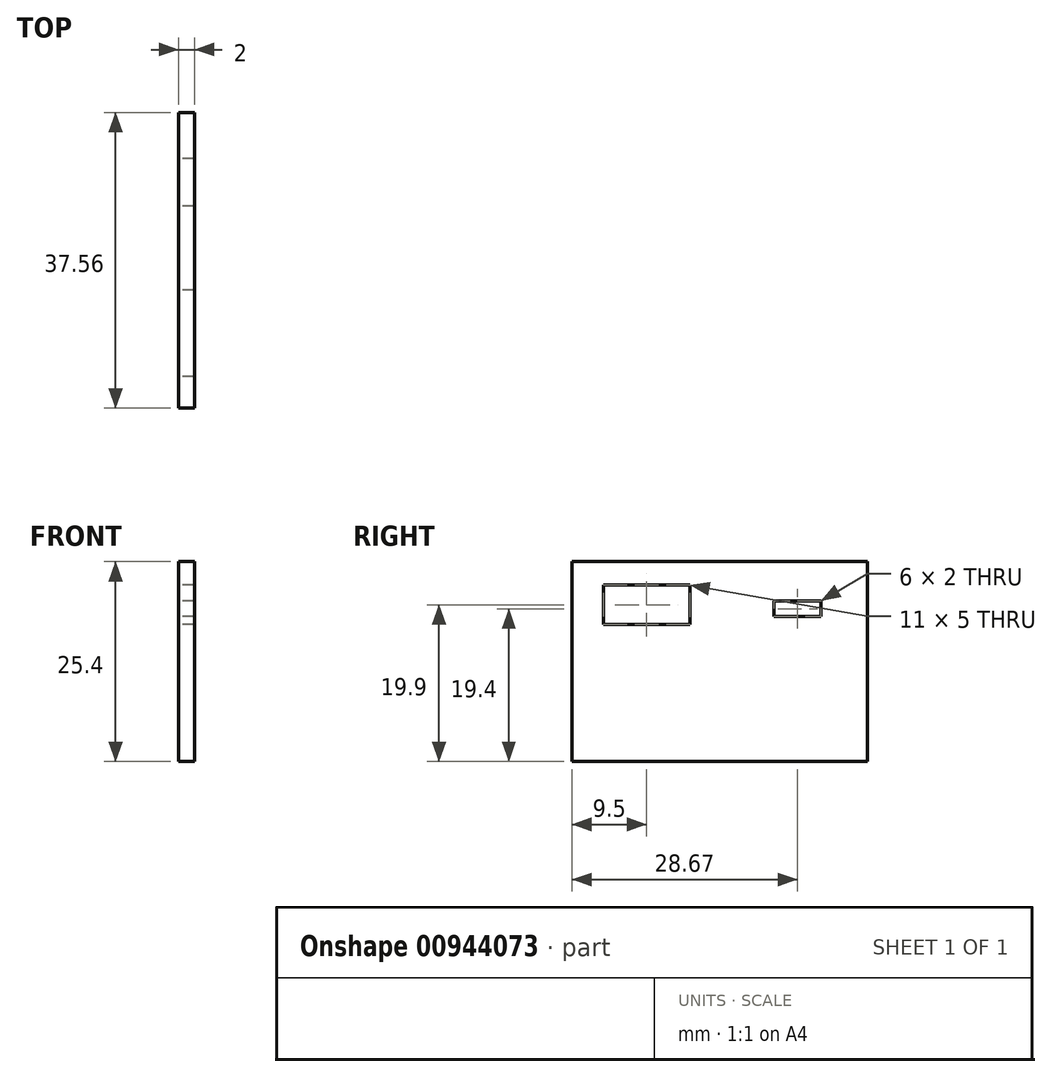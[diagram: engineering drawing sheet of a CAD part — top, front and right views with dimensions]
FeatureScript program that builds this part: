
annotation { "Feature Type Name" : "Feature", "Feature Type Description" : "" }
export const myFeature = defineFeature(function(context is Context, id is Id, definition is map)
    precondition{}
    {
        {
            var Q0;
            Q0=qCreatedBy(makeId("Right.planeOp"),FACE);
            var sketch = newSketch(context, id + "F0", { "sketchPlane" : qUnion([Q0])});
            skLineSegment(sketch, "E0.bottom", {"start": v(0, 25.4) * mm, "end": v(37.56, 25.4) * mm});
            skLineSegment(sketch, "E0.top", {"start": v(0, 0) * mm, "end": v(37.56, 0) * mm});
            skLineSegment(sketch, "E0.left", {"start": v(0, 25.4) * mm, "end": v(0, 0) * mm});
            skLineSegment(sketch, "E0.right", {"start": v(37.56, 25.4) * mm, "end": v(37.56, 0) * mm});
            skLineSegment(sketch, "E1.bottom", {"start": v(4, 22.4) * mm, "end": v(15, 22.4) * mm});
            skLineSegment(sketch, "E1.top", {"start": v(4, 17.4) * mm, "end": v(15, 17.4) * mm});
            skLineSegment(sketch, "E1.left", {"start": v(4, 22.4) * mm, "end": v(4, 17.4) * mm});
            skLineSegment(sketch, "E1.right", {"start": v(15, 22.4) * mm, "end": v(15, 17.4) * mm});
            skLineSegment(sketch, "E2.bottom", {"start": v(25.67, 20.4) * mm, "end": v(31.67, 20.4) * mm});
            skLineSegment(sketch, "E2.top", {"start": v(25.67, 18.4) * mm, "end": v(31.67, 18.4) * mm});
            skLineSegment(sketch, "E2.left", {"start": v(25.67, 20.4) * mm, "end": v(25.67, 18.4) * mm});
            skLineSegment(sketch, "E2.right", {"start": v(31.67, 20.4) * mm, "end": v(31.67, 18.4) * mm});
            skSolve(sketch);
        }
        {
            var Q0;
            Q0=makeQuery(id+"F0.imprint","IMPRINT",FACE,{"disambiguationData":[TD([[makeQuery(id+"F0.imprint","IMPRINT",EDGE,{"derivedFrom":sQuery(id+"F0.wireOp",EDGE,"E0.bottom")}),-1.0]])]});
            extrude(context, id + "F1", {"entities" : qUnion([Q0]), "depth" : 2 * mm, "offsetDistance" : 25 * mm});
        }
    });
